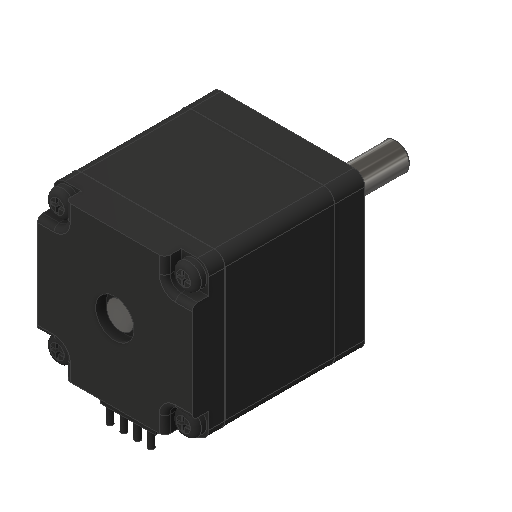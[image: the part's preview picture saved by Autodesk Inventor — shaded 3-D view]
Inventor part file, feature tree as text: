
AUTODESK INVENTOR PART (.ipt)
format: ipt  version: 2025 (Build 290162010, 162A)  size: 549,376 bytes
history: native  units: mm
features: fillet x1
ambient origin geometry x8: Origin, YZ Plane, XZ Plane, XY Plane, X Axis, Y Axis, Z Axis, Center Point
bodies: Solid1 (feature_tree)
feature tree (1):
  fillet  "Fillet3"  [1 undecoded]
note: 1 required parameter value undecoded (feature->parameter linkage not recoverable at this tier; creation-order binding heuristic only, values carry confidence <= 0.55)
